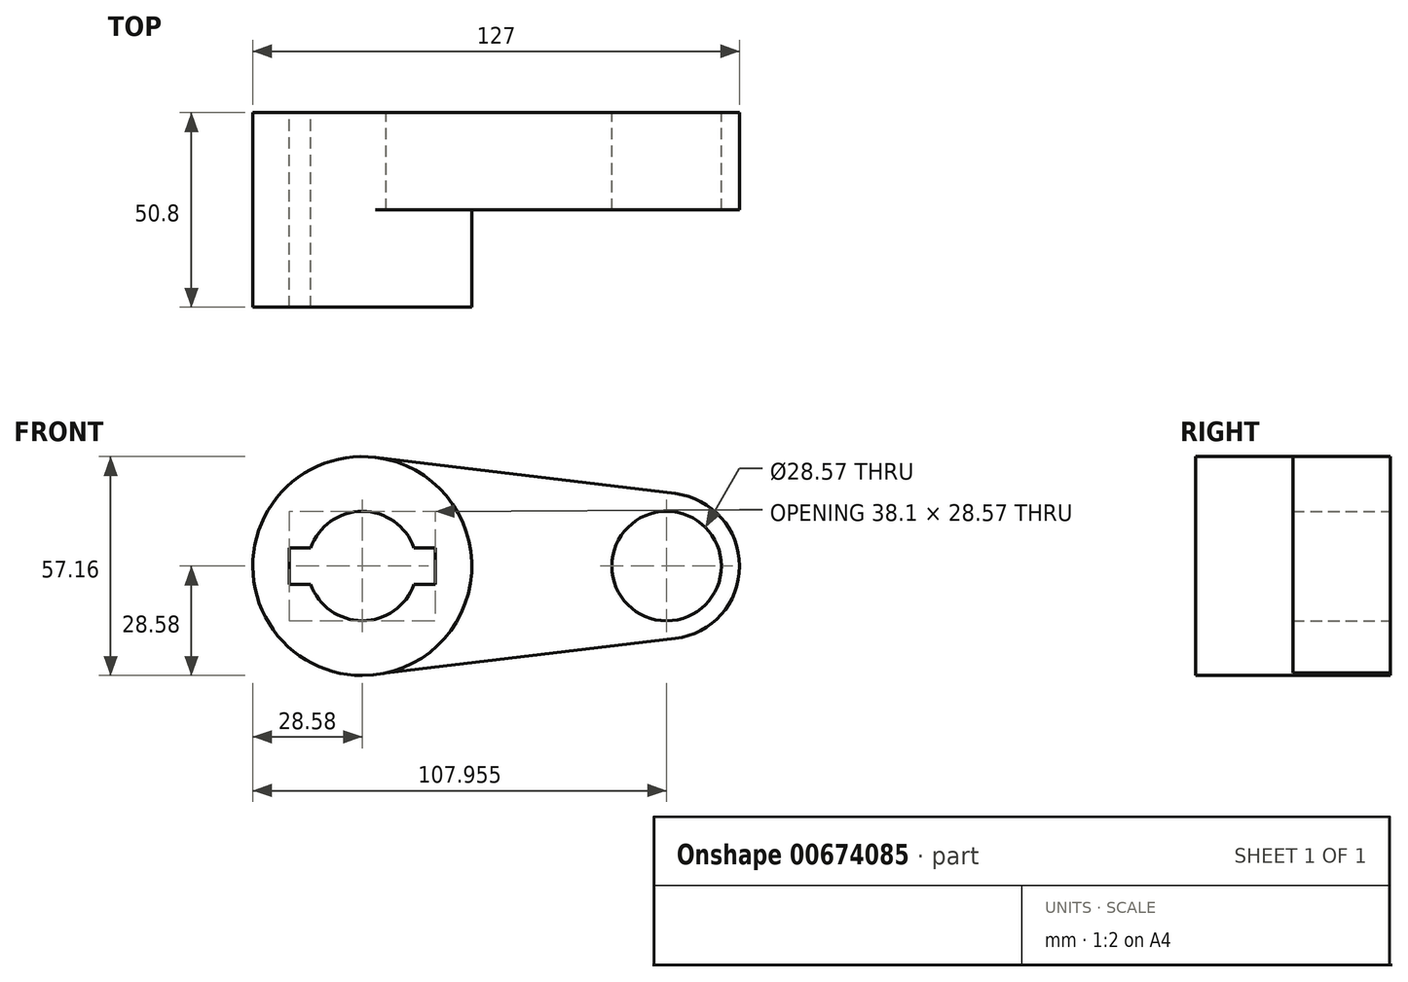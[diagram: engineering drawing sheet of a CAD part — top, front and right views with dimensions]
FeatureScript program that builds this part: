
annotation { "Feature Type Name" : "Feature", "Feature Type Description" : "" }
export const myFeature = defineFeature(function(context is Context, id is Id, definition is map)
    precondition{}
    {
        {
            var Q0;
            Q0=qCreatedBy(makeId("Front.planeOp"),FACE);
            var sketch = newSketch(context, id + "F0", { "sketchPlane" : qUnion([Q0])});
            skCircle(sketch, "E0", {"center": v(0, 0) * mm, "radius": 28.58 * mm});
            skCircle(sketch, "E1", {"center": v(79.38, 0) * mm, "radius": 19.05 * mm});
            skLineSegment(sketch, "E2", {"start": v(3.43, 28.37) * mm, "end": v(81.66, 18.91) * mm});
            skLineSegment(sketch, "E3", {"start": v(6.19, -27.9) * mm, "end": v(81.63, -18.92) * mm});
            skCircle(sketch, "E4", {"center": v(0, 0) * mm, "radius": 14.29 * mm});
            skCircle(sketch, "E5", {"center": v(79.38, 0) * mm, "radius": 14.29 * mm});
            skLineSegment(sketch, "E6.bottom", {"start": v(-19.05, -4.76) * mm, "end": v(19.05, -4.76) * mm});
            skLineSegment(sketch, "E6.top", {"start": v(-19.05, 4.76) * mm, "end": v(19.05, 4.76) * mm});
            skLineSegment(sketch, "E6.left", {"start": v(-19.05, -4.76) * mm, "end": v(-19.05, 4.76) * mm});
            skLineSegment(sketch, "E6.right", {"start": v(19.05, -4.76) * mm, "end": v(19.05, 4.76) * mm});
            skSolve(sketch);
        }
        {
            var Q0;
            {var subQ7=sQuery(id+"F0.wireOp",EDGE,"E6.left");Q0=makeQuery(id+"F0.imprint","IMPRINT",FACE,{"disambiguationData":[TD([[makeQuery(id+"F0.imprint","IMPRINT",EDGE,{"derivedFrom":subQ7}),1.0]])]});}
            var Q1;
            {var subQ0=sQuery(id+"F0.wireOp",EDGE,"E2");Q1=makeQuery(id+"F0.imprint","IMPRINT",FACE,{"disambiguationData":[TD([[makeQuery(id+"F0.imprint","IMPRINT",EDGE,{"derivedFrom":subQ0}),-1.0]])]});}
            var Q2;
            Q2=makeQuery(id+"F0.imprint","IMPRINT",FACE,{"disambiguationData":[TD([[makeQuery(id+"F0.imprint","IMPRINT",EDGE,{"derivedFrom":sQuery(id+"F0.wireOp",EDGE,"E5")}),-1.0]])]});
            extrude(context, id + "F1", {"entities" : qUnion([Q0, Q1, Q2]), "depth" : 25.4 * mm, "offsetDistance" : 25.4 * mm});
        }
        {
            var Q0;
            {var subQ7=sQuery(id+"F0.wireOp",EDGE,"E6.left");Q0=makeQuery(id+"F0.imprint","IMPRINT",FACE,{"disambiguationData":[TD([[makeQuery(id+"F0.imprint","IMPRINT",EDGE,{"derivedFrom":subQ7}),1.0]])]});}
            extrude(context, id + "F2", {"entities" : qUnion([Q0]), "operationType" : NewBodyOperationType.ADD, "depth" : 50.8 * mm, "offsetDistance" : 25.4 * mm});
        }
    });
